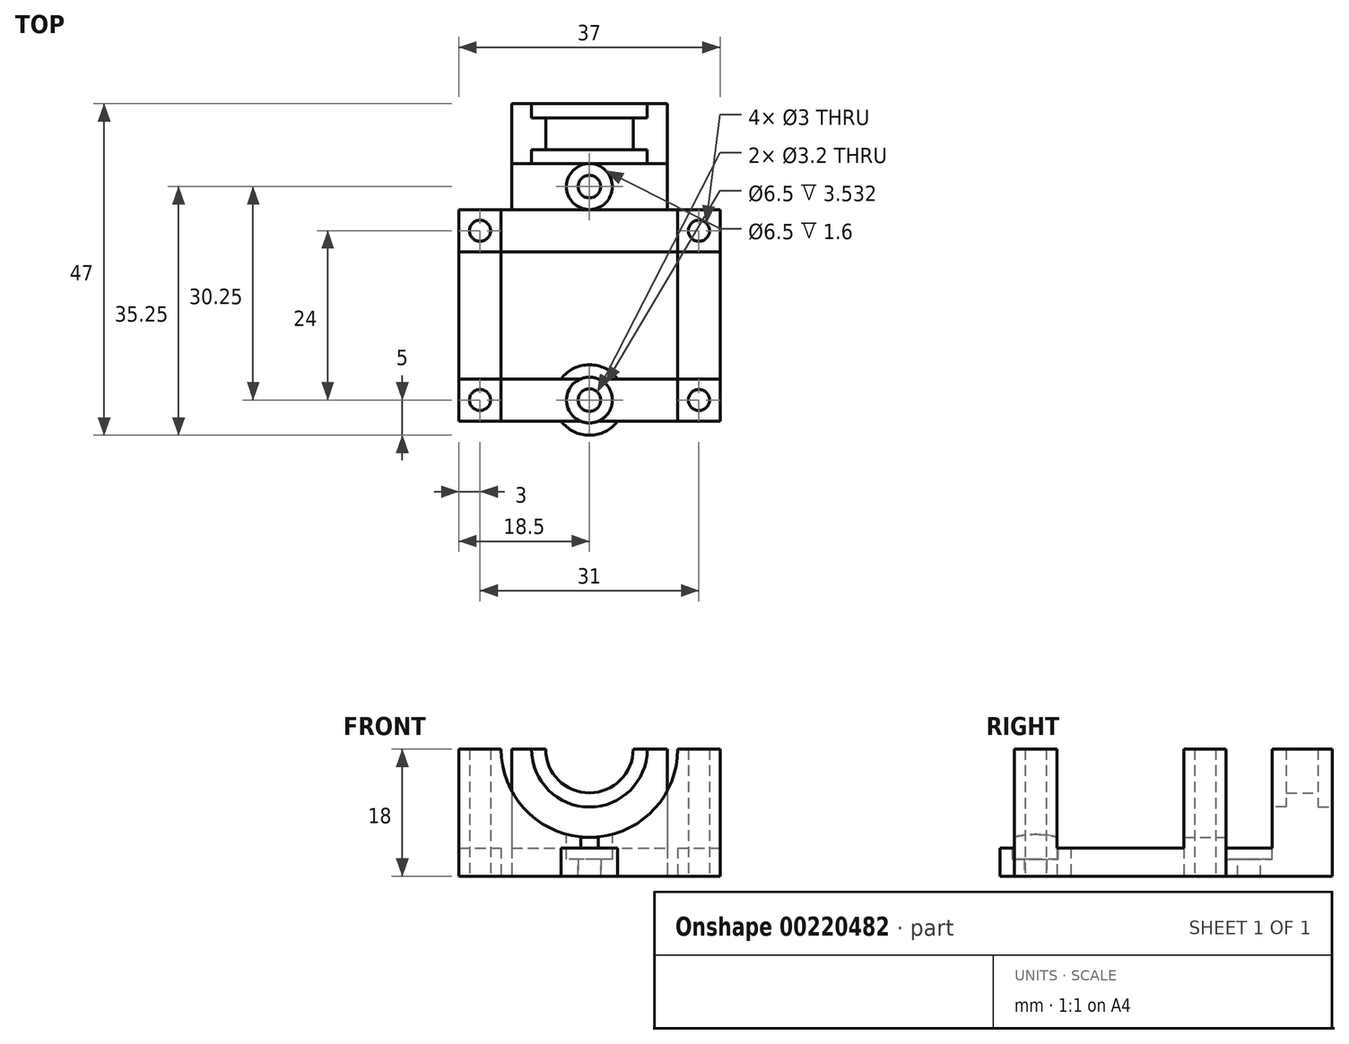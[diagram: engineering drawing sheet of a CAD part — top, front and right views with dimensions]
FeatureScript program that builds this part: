
annotation { "Feature Type Name" : "Feature", "Feature Type Description" : "" }
export const myFeature = defineFeature(function(context is Context, id is Id, definition is map)
    precondition{}
    {
        {
            var Q0;
            Q0=qCreatedBy(makeId("Top.planeOp"),FACE);
            var sketch = newSketch(context, id + "F0", { "sketchPlane" : qUnion([Q0])});
            skLineSegment(sketch, "E0", {"start": v(0, 0) * mm, "end": v(0, 45) * mm, "construction": true});
            skLineSegment(sketch, "E1", {"start": v(18.5, 0) * mm, "end": v(18.5, 30) * mm});
            skLineSegment(sketch, "E2", {"start": v(18.5, 30) * mm, "end": v(11, 30) * mm});
            skLineSegment(sketch, "E3", {"start": v(11, 30) * mm, "end": v(11, 45) * mm});
            skLineSegment(sketch, "E4", {"start": v(11, 45) * mm, "end": v(-11, 45) * mm});
            skLineSegment(sketch, "E5", {"start": v(-11, 45) * mm, "end": v(-11, 30) * mm});
            skLineSegment(sketch, "E6", {"start": v(-11, 30) * mm, "end": v(-18.5, 30) * mm});
            skLineSegment(sketch, "E7", {"start": v(-18.5, 30) * mm, "end": v(-18.5, 0) * mm});
            skLineSegment(sketch, "E8.bottom", {"start": v(-12.5, 24) * mm, "end": v(12.5, 24) * mm});
            skLineSegment(sketch, "E8.left", {"start": v(-12.5, 24) * mm, "end": v(-12.5, 6) * mm});
            skLineSegment(sketch, "E8.right", {"start": v(12.5, 24) * mm, "end": v(12.5, 6) * mm});
            skArc(sketch, "E9", {"start": v(-4, 6) * mm, "mid": v(0, 8) * mm, "end": v(4, 6) * mm});
            skArc(sketch, "E10", {"start": v(-4, 0) * mm, "mid": v(0, -2) * mm, "end": v(4, 0) * mm});
            skPoint(sketch, "E11", {"position": v(0, 24) * mm});
            skLineSegment(sketch, "E12", {"start": v(-18.5, 0) * mm, "end": v(18.5, 0) * mm, "construction": true});
            skLineSegment(sketch, "E13", {"start": v(-12.5, 6) * mm, "end": v(12.5, 6) * mm, "construction": true});
            skLineSegment(sketch, "E14", {"start": v(-12.5, 6) * mm, "end": v(-4, 6) * mm});
            skLineSegment(sketch, "E15", {"start": v(4, 6) * mm, "end": v(12.5, 6) * mm});
            skLineSegment(sketch, "E16", {"start": v(18.5, 0) * mm, "end": v(4, 0) * mm});
            skLineSegment(sketch, "E17", {"start": v(-4, 0) * mm, "end": v(-18.5, 0) * mm});
            skLineSegment(sketch, "E18", {"start": v(-12.5, 0) * mm, "end": v(12.5, 6) * mm, "construction": true});
            skSolve(sketch);
        }
        {
            var Q0;
            Q0 = qSketchRegion(id + "F0", true);
            extrude(context, id + "F1", {"entities" : qUnion([Q0]), "depth" : 4 * mm});
        }
        {
            var Q0;
            Q0=makeQuery(id+"F1.opExtrude","CAP_FACE",FACE,{"disambiguationData":[OSD([sQuery(id+"F0.wireOp",EDGE,"U9dfoCG1-PFxA-Uhlo-kPHr-zTRKNoq8szU0"),sQuery(id+"F0.wireOp",EDGE,"E1"),sQuery(id+"F0.wireOp",EDGE,"E2"),sQuery(id+"F0.wireOp",EDGE,"E3"),sQuery(id+"F0.wireOp",EDGE,"E4"),sQuery(id+"F0.wireOp",EDGE,"E5"),sQuery(id+"F0.wireOp",EDGE,"E6"),sQuery(id+"F0.wireOp",EDGE,"E7"),sQuery(id+"F0.wireOp",EDGE,"E8.bottom"),sQuery(id+"F0.wireOp",EDGE,"E8.top"),sQuery(id+"F0.wireOp",EDGE,"E8.left"),sQuery(id+"F0.wireOp",EDGE,"E8.right")])],"isStart":false});
            var sketch = newSketch(context, id + "F2", { "sketchPlane" : qUnion([Q0])});
            skLineSegment(sketch, "E19.bottom", {"start": v(-11, 45) * mm, "end": v(11, 45) * mm});
            skLineSegment(sketch, "E19.top", {"start": v(-11, 36.5) * mm, "end": v(11, 36.5) * mm});
            skLineSegment(sketch, "E19.left", {"start": v(-11, 45) * mm, "end": v(-11, 36.5) * mm});
            skLineSegment(sketch, "E19.right", {"start": v(11, 45) * mm, "end": v(11, 36.5) * mm});
            skLineSegment(sketch, "E20.bottom", {"start": v(-18.5, 30) * mm, "end": v(18.5, 30) * mm});
            skLineSegment(sketch, "E20.top", {"start": v(-18.5, 24) * mm, "end": v(18.5, 24) * mm});
            skLineSegment(sketch, "E20.left", {"start": v(-18.5, 30) * mm, "end": v(-18.5, 24) * mm});
            skLineSegment(sketch, "E20.right", {"start": v(18.5, 30) * mm, "end": v(18.5, 24) * mm});
            skLineSegment(sketch, "E21.left", {"start": v(-18.5, 24) * mm, "end": v(-18.5, 30) * mm});
            skLineSegment(sketch, "E21.right", {"start": v(18.5, 24) * mm, "end": v(18.5, 30) * mm});
            skLineSegment(sketch, "E22.bottom", {"start": v(-18.5, 0) * mm, "end": v(18.5, 0) * mm});
            skLineSegment(sketch, "E22.top", {"start": v(-18.5, 6) * mm, "end": v(18.5, 6) * mm});
            skLineSegment(sketch, "E22.left", {"start": v(-18.5, 0) * mm, "end": v(-18.5, 6) * mm});
            skLineSegment(sketch, "E22.right", {"start": v(18.5, 0) * mm, "end": v(18.5, 6) * mm});
            skSolve(sketch);
        }
        {
            var Q0;
            Q0 = qSketchRegion(id + "F2", true);
            extrude(context, id + "F3", {"entities" : qUnion([Q0]), "operationType" : NewBodyOperationType.ADD, "depth" : 14 * mm});
        }
        {
            var Q0;
            Q0=makeQuery(id+"F3.boolean.opBoolean","MERGE",FACE,{"derivedFrom":[makeQuery(id+"F1.opExtrude","SWEPT_FACE",FACE,{"disambiguationData":[OSD([sQuery(id+"F0.wireOp",EDGE,"E4")])]}),makeQuery(id+"F3.opExtrude","SWEPT_FACE",FACE,{"disambiguationData":[OSD([sQuery(id+"F2.wireOp",EDGE,"E19.bottom")])]})]});
            var sketch = newSketch(context, id + "F4", { "sketchPlane" : qUnion([Q0])});
            skCircle(sketch, "E23", {"center": v(0, 18) * mm, "radius": 6.2 * mm});
            skSolve(sketch);
        }
        {
            var Q0;
            Q0 = qSketchRegion(id + "F4", true);
            extrude(context, id + "F5", {"entities" : qUnion([Q0]), "operationType" : NewBodyOperationType.REMOVE, "endBound" : BoundingType.UP_TO_NEXT, "oppositeDirection" : true, "depth" : 25 * mm});
        }
        {
            var Q0;
            Q0=makeQuery(id+"F3.boolean.opBoolean","MERGE",FACE,{"derivedFrom":[makeQuery(id+"F1.opExtrude","SWEPT_FACE",FACE,{"disambiguationData":[OSD([sQuery(id+"F0.wireOp",EDGE,"E2")])]}),makeQuery(id+"F1.opExtrude","SWEPT_FACE",FACE,{"disambiguationData":[OSD([sQuery(id+"F0.wireOp",EDGE,"E6")])]}),makeQuery(id+"F3.opExtrude","SWEPT_FACE",FACE,{"disambiguationData":[OSD([sQuery(id+"F2.wireOp",EDGE,"E20.bottom")])]})]});
            var sketch = newSketch(context, id + "F6", { "sketchPlane" : qUnion([Q0])});
            skCircle(sketch, "E24", {"center": v(0, 18) * mm, "radius": 12.5 * mm});
            skSolve(sketch);
        }
        {
            var Q0;
            Q0 = qSketchRegion(id + "F6", true);
            extrude(context, id + "F7", {"entities" : qUnion([Q0]), "operationType" : NewBodyOperationType.REMOVE, "endBound" : BoundingType.THROUGH_ALL, "oppositeDirection" : true, "depth" : 25 * mm});
        }
        {
            var Q0;
            Q0=makeQuery(id+"F3.boolean.opBoolean","MERGE",FACE,{"derivedFrom":[makeQuery(id+"F1.opExtrude","SWEPT_FACE",FACE,{"disambiguationData":[OSD([sQuery(id+"F0.wireOp",EDGE,"E4")])]}),makeQuery(id+"F3.opExtrude","SWEPT_FACE",FACE,{"disambiguationData":[OSD([sQuery(id+"F2.wireOp",EDGE,"E19.bottom")])]})]});
            var sketch = newSketch(context, id + "F8", { "sketchPlane" : qUnion([Q0])});
            skLineSegment(sketch, "E25", {"start": v(-11, 18) * mm, "end": v(11, 18) * mm, "construction": true});
            skCircle(sketch, "E26", {"center": v(0, 18) * mm, "radius": 8.2 * mm});
            skSolve(sketch);
        }
        {
            var Q0;
            Q0 = qSketchRegion(id + "F8", true);
            extrude(context, id + "F9", {"entities" : qUnion([Q0]), "operationType" : NewBodyOperationType.REMOVE, "oppositeDirection" : true, "depth" : 2 * mm});
        }
        {
            var Q0;
            Q0=makeQuery(id+"F3.opExtrude","SWEPT_FACE",FACE,{"disambiguationData":[OSD([sQuery(id+"F2.wireOp",EDGE,"E19.top")])]});
            var sketch = newSketch(context, id + "F10", { "sketchPlane" : qUnion([Q0])});
            skLineSegment(sketch, "E27", {"start": v(11, 18) * mm, "end": v(-11, 18) * mm, "construction": true});
            skCircle(sketch, "E28", {"center": v(0, 18) * mm, "radius": 8.2 * mm});
            skSolve(sketch);
        }
        {
            var Q0;
            Q0 = qSketchRegion(id + "F10", true);
            extrude(context, id + "F11", {"entities" : qUnion([Q0]), "operationType" : NewBodyOperationType.REMOVE, "oppositeDirection" : true, "depth" : 2 * mm});
        }
        {
            var Q0;
            Q0=makeQuery(id+"F1.opExtrude","CAP_FACE",FACE,{"disambiguationData":[OSD([sQuery(id+"F0.wireOp",EDGE,"U9dfoCG1-PFxA-Uhlo-kPHr-zTRKNoq8szU0"),sQuery(id+"F0.wireOp",EDGE,"E1"),sQuery(id+"F0.wireOp",EDGE,"E2"),sQuery(id+"F0.wireOp",EDGE,"E3"),sQuery(id+"F0.wireOp",EDGE,"E4"),sQuery(id+"F0.wireOp",EDGE,"E5"),sQuery(id+"F0.wireOp",EDGE,"E6"),sQuery(id+"F0.wireOp",EDGE,"E7"),sQuery(id+"F0.wireOp",EDGE,"E8.bottom"),sQuery(id+"F0.wireOp",EDGE,"E8.top"),sQuery(id+"F0.wireOp",EDGE,"E8.left"),sQuery(id+"F0.wireOp",EDGE,"E8.right")])],"isStart":true});
            var sketch = newSketch(context, id + "F12", { "sketchPlane" : qUnion([Q0])});
            skLineSegment(sketch, "E29", {"start": v(-18.5, -30) * mm, "end": v(-12.5, -24) * mm, "construction": true});
            skLineSegment(sketch, "E30", {"start": v(18.5, 0) * mm, "end": v(18.15, -0.01) * mm, "construction": true});
            skLineSegment(sketch, "E31", {"start": v(-18.5, -30) * mm, "end": v(-18.15, -29.77) * mm, "construction": true});
            skLineSegment(sketch, "E32.bottom", {"start": v(-15.5, -27) * mm, "end": v(15.5, -27) * mm, "construction": true});
            skLineSegment(sketch, "E32.top", {"start": v(-15.5, -3) * mm, "end": v(15.5, -3) * mm, "construction": true});
            skLineSegment(sketch, "E32.left", {"start": v(-15.5, -27) * mm, "end": v(-15.5, -3) * mm, "construction": true});
            skLineSegment(sketch, "E32.right", {"start": v(15.5, -27) * mm, "end": v(15.5, -3) * mm, "construction": true});
            skLineSegment(sketch, "E33", {"start": v(12.5, -6) * mm, "end": v(18.5, 0) * mm, "construction": true});
            skCircle(sketch, "E34", {"center": v(-15.5, -27) * mm, "radius": 1.5 * mm});
            skCircle(sketch, "E35", {"center": v(15.5, -27) * mm, "radius": 1.5 * mm});
            skCircle(sketch, "E36", {"center": v(15.5, -3) * mm, "radius": 1.5 * mm});
            skCircle(sketch, "E37", {"center": v(-15.5, -3) * mm, "radius": 1.5 * mm});
            skSolve(sketch);
        }
        {
            var Q0;
            Q0 = qSketchRegion(id + "F12", true);
            extrude(context, id + "F13", {"entities" : qUnion([Q0]), "operationType" : NewBodyOperationType.REMOVE, "endBound" : BoundingType.THROUGH_ALL, "oppositeDirection" : true, "depth" : 25 * mm});
        }
        {
            var Q0;
            {var subQ0=sQuery(id+"F0.wireOp",EDGE,"E6");var subQ1=sQuery(id+"F0.wireOp",EDGE,"E5");var subQ2=sQuery(id+"F0.wireOp",EDGE,"E3");var subQ3=sQuery(id+"F0.wireOp",EDGE,"E2");Q0=makeQuery(id+"F3.boolean.opBoolean","SPLIT",FACE,{"disambiguationData":[TD([makeQuery(id+"F1.opExtrude","SWEPT_FACE",FACE,{"disambiguationData":[OSD([subQ3])]})])],"derivedFrom":makeQuery(id+"F1.opExtrude","CAP_FACE",FACE,{"disambiguationData":[OSD([sQuery(id+"F0.wireOp",EDGE,"U9dfoCG1-PFxA-Uhlo-kPHr-zTRKNoq8szU0"),sQuery(id+"F0.wireOp",EDGE,"E1"),subQ3,subQ2,sQuery(id+"F0.wireOp",EDGE,"E4"),subQ1,subQ0,sQuery(id+"F0.wireOp",EDGE,"E7"),sQuery(id+"F0.wireOp",EDGE,"E8.bottom"),sQuery(id+"F0.wireOp",EDGE,"E8.top"),sQuery(id+"F0.wireOp",EDGE,"E8.left"),sQuery(id+"F0.wireOp",EDGE,"E8.right")])],"isStart":false})});}
            var sketch = newSketch(context, id + "F14", { "sketchPlane" : qUnion([Q0])});
            skLineSegment(sketch, "E38", {"start": v(-11, 36.5) * mm, "end": v(11, 30) * mm, "construction": true});
            skCircle(sketch, "E39", {"center": v(0, 33.25) * mm, "radius": 1.6 * mm});
            skSolve(sketch);
        }
        {
            var Q0;
            Q0 = qSketchRegion(id + "F14", true);
            extrude(context, id + "F15", {"entities" : qUnion([Q0]), "operationType" : NewBodyOperationType.REMOVE, "endBound" : BoundingType.UP_TO_NEXT, "oppositeDirection" : true, "depth" : 25 * mm});
        }
        {
            var Q0;
            Q0=makeQuery(id+"F1.opExtrude","CAP_FACE",FACE,{"disambiguationData":[OSD([sQuery(id+"F0.wireOp",EDGE,"U9dfoCG1-PFxA-Uhlo-kPHr-zTRKNoq8szU0"),sQuery(id+"F0.wireOp",EDGE,"E1"),sQuery(id+"F0.wireOp",EDGE,"E2"),sQuery(id+"F0.wireOp",EDGE,"E3"),sQuery(id+"F0.wireOp",EDGE,"E4"),sQuery(id+"F0.wireOp",EDGE,"E5"),sQuery(id+"F0.wireOp",EDGE,"E6"),sQuery(id+"F0.wireOp",EDGE,"E7"),sQuery(id+"F0.wireOp",EDGE,"E8.bottom"),sQuery(id+"F0.wireOp",EDGE,"E8.top"),sQuery(id+"F0.wireOp",EDGE,"E8.left"),sQuery(id+"F0.wireOp",EDGE,"E8.right")])],"isStart":true});
            var sketch = newSketch(context, id + "F16", { "sketchPlane" : qUnion([Q0])});
            skLineSegment(sketch, "E40", {"start": v(15.5, -3) * mm, "end": v(-15.5, -3) * mm, "construction": true});
            skCircle(sketch, "E41", {"center": v(0, -3) * mm, "radius": 1.6 * mm});
            skSolve(sketch);
        }
        {
            var Q0;
            Q0 = qSketchRegion(id + "F16", true);
            extrude(context, id + "F17", {"entities" : qUnion([Q0]), "operationType" : NewBodyOperationType.REMOVE, "endBound" : BoundingType.THROUGH_ALL, "oppositeDirection" : true, "depth" : 25 * mm});
        }
        {
            var Q0;
            {var subQ0=sQuery(id+"F0.wireOp",EDGE,"E9");var subQ1=sQuery(id+"F0.wireOp",EDGE,"E14");var subQ2=sQuery(id+"F0.wireOp",EDGE,"E15");var subQ3=sQuery(id+"F0.wireOp",EDGE,"E17");var subQ4=sQuery(id+"F0.wireOp",EDGE,"E16");var subQ5=sQuery(id+"F0.wireOp",EDGE,"E10");var subQ6=makeQuery(id+"F1.opExtrude","CAP_FACE",FACE,{"disambiguationData":[OSD([sQuery(id+"F0.wireOp",EDGE,"E1"),sQuery(id+"F0.wireOp",EDGE,"E2"),sQuery(id+"F0.wireOp",EDGE,"E3"),sQuery(id+"F0.wireOp",EDGE,"E4"),sQuery(id+"F0.wireOp",EDGE,"E5"),sQuery(id+"F0.wireOp",EDGE,"E6"),sQuery(id+"F0.wireOp",EDGE,"E7"),sQuery(id+"F0.wireOp",EDGE,"E8.bottom"),sQuery(id+"F0.wireOp",EDGE,"E8.left"),sQuery(id+"F0.wireOp",EDGE,"E8.right"),subQ0,subQ5,subQ1,subQ2,subQ4,subQ3])],"isStart":false});Q0=makeQuery(id+"Fl3KebhsqYtVvOP_1.boolean.opBoolean","MERGE",FACE,{"derivedFrom":[makeQuery(id+"F3.boolean.opBoolean","SPLIT",FACE,{"disambiguationData":[TD([makeQuery(id+"F1.opExtrude","SWEPT_FACE",FACE,{"disambiguationData":[OSD([subQ5])]})])],"derivedFrom":subQ6}),makeQuery(id+"F3.boolean.opBoolean","SPLIT",FACE,{"disambiguationData":[TD([makeQuery(id+"F1.opExtrude","SWEPT_FACE",FACE,{"disambiguationData":[OSD([subQ0])]})])],"derivedFrom":subQ6}),makeQuery(id+"Fl3KebhsqYtVvOP_1.opExtrude","CAP_FACE",FACE,{"disambiguationData":[OSD([sQuery(id+"Ftvz46sSMqKDkQk_1.wireOp",EDGE,"U13BRWaf-ylfx-tRFh-Kczm-vth2rIo6frmx")])],"isStart":true})]});}
            var sketch = newSketch(context, id + "F18", { "sketchPlane" : qUnion([Q0])});
            skCircle(sketch, "E42", {"center": v(0, 3) * mm, "radius": 3.25 * mm});
            skCircle(sketch, "E43", {"center": v(0, 33.25) * mm, "radius": 3.25 * mm});
            skSolve(sketch);
        }
        {
            var Q0;
            Q0 = qSketchRegion(id + "F18", true);
            extrude(context, id + "F19", {"entities" : qUnion([Q0]), "operationType" : NewBodyOperationType.REMOVE, "oppositeDirection" : true, "depth" : 1.6 * mm});
        }
        {
            var Q0;
            Q0=makeQuery(id+"F19.boolean.opBoolean","COPY",FACE,{"derivedFrom":makeQuery(id+"F19.opExtrude","CAP_FACE",FACE,{"disambiguationData":[OSD([sQuery(id+"F18.wireOp",EDGE,"E42")])],"isStart":false})});
            var sketch = newSketch(context, id + "F20", { "sketchPlane" : qUnion([Q0])});
            skCircle(sketch, "E44", {"center": v(0, 3) * mm, "radius": 3.25 * mm});
            skSolve(sketch);
        }
        {
            var Q0;
            Q0 = qSketchRegion(id + "F20", true);
            var Q1;
            {var subQ0=sQuery(id+"F2.wireOp",EDGE,"E20.bottom");var subQ1=sQuery(id+"F2.wireOp",EDGE,"E20.top");var subQ2=sQuery(id+"F2.wireOp",EDGE,"E21.left");Q1=makeQuery(id+"F7.boolean.opBoolean","SPLIT",FACE,{"disambiguationData":[TD([makeQuery(id+"F1.opExtrude","SWEPT_FACE",FACE,{"disambiguationData":[OSD([sQuery(id+"F0.wireOp",EDGE,"E7")])]})])],"derivedFrom":makeQuery(id+"F3.opExtrude","CAP_FACE",FACE,{"disambiguationData":[OSD([subQ0,subQ1,subQ2,sQuery(id+"F2.wireOp",EDGE,"E21.right")])],"isStart":false})});}
            extrude(context, id + "F21", {"entities" : qUnion([Q0]), "operationType" : NewBodyOperationType.REMOVE, "endBound" : BoundingType.UP_TO_SURFACE, "endBoundEntityFace" : qUnion([Q1]), "depth" : 25 * mm});
        }
    });
